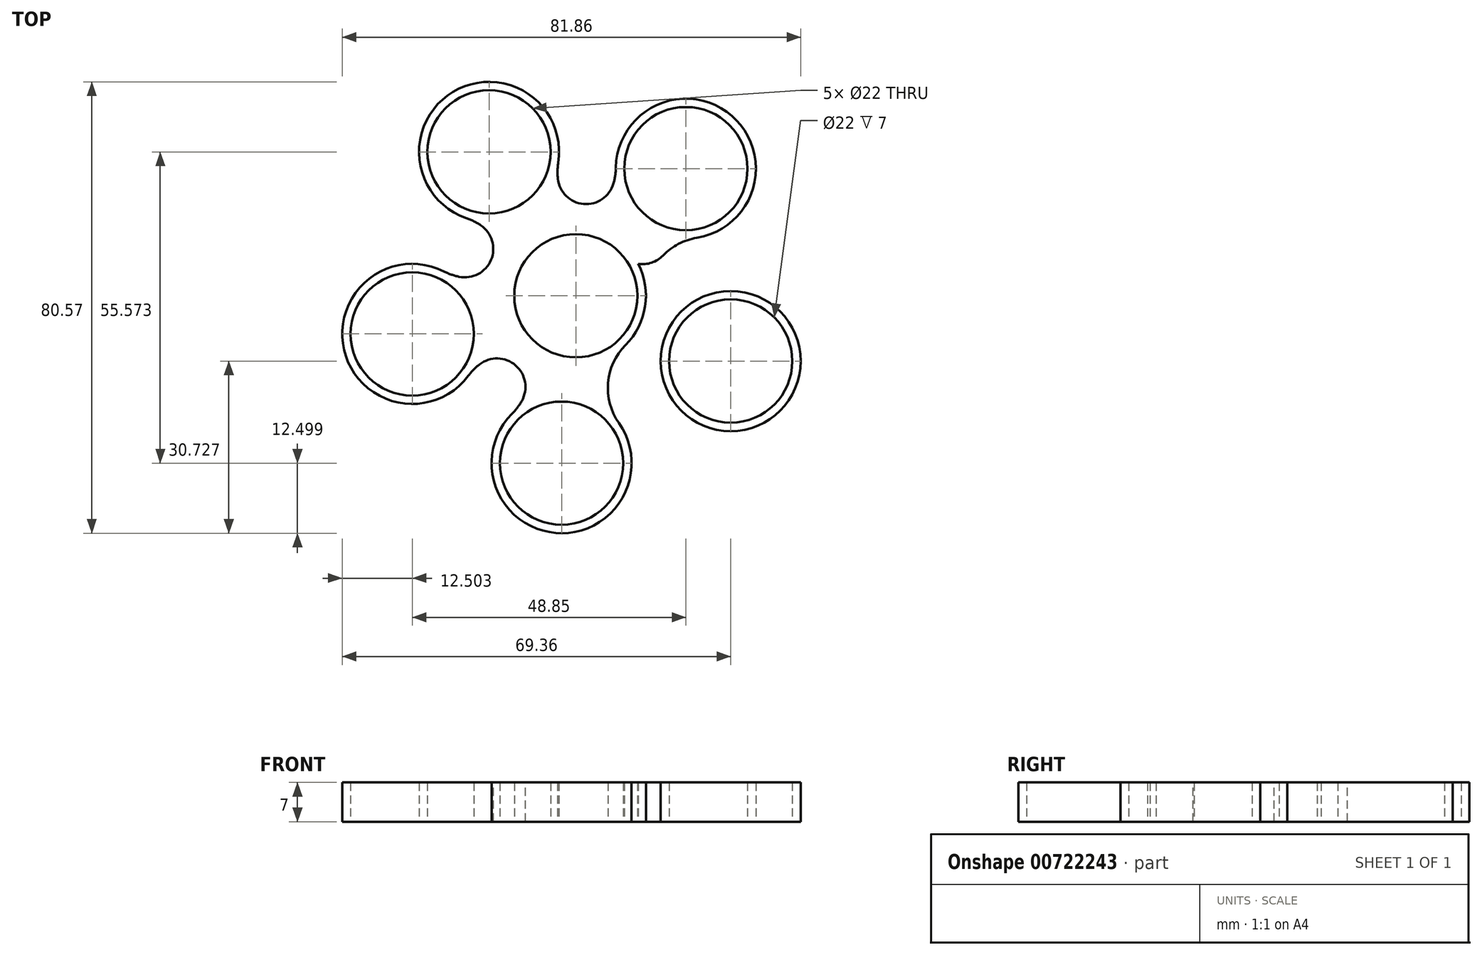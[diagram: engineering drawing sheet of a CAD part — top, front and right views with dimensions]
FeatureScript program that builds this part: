
annotation { "Feature Type Name" : "Feature", "Feature Type Description" : "" }
export const myFeature = defineFeature(function(context is Context, id is Id, definition is map)
    precondition{}
    {
        {
            var Q0;
            Q0=qCreatedBy(makeId("Top.planeOp"),FACE);
            var sketch = newSketch(context, id + "F0", { "sketchPlane" : qUnion([Q0])});
            skCircle(sketch, "E0", {"center": v(0, 0) * mm, "radius": 12.5 * mm});
            skCircle(sketch, "E1", {"center": v(19.63, 22.68) * mm, "radius": 12.5 * mm});
            skLineSegment(sketch, "E2", {"start": v(19.63, 22.68) * mm, "end": v(7.14, 22.87) * mm});
            skLineSegment(sketch, "E3", {"start": v(19.63, 22.68) * mm, "end": v(21.62, 10.34) * mm});
            skLineSegment(sketch, "E4", {"start": v(0, 0) * mm, "end": v(19.63, 22.68) * mm});
            skLineSegment(sketch, "E5", {"start": v(0, 0) * mm, "end": v(12.5, -0.2) * mm});
            skArc(sketch, "E6", {"start": v(21.62, 10.34) * mm, "mid": v(15.14, 6.73) * mm, "end": v(12.5, -0.2) * mm});
            skArc(sketch, "E7.MirrorCS", {"start": v(7.14, 22.87) * mm, "mid": v(4.5, 15.95) * mm, "end": v(-1.98, 12.34) * mm});
            skCircle(sketch, "E8", {"center": v(0, 0) * mm, "radius": 11 * mm});
            skCircle(sketch, "E9", {"center": v(19.63, 22.68) * mm, "radius": 11 * mm});
            skCircle(sketch, "E10.1.0", {"center": v(-15.5, 25.68) * mm, "radius": 11 * mm});
            skCircle(sketch, "E10.1.1", {"center": v(-15.5, 25.68) * mm, "radius": 12.5 * mm});
            skArc(sketch, "E10.1.2", {"start": v(-3.16, 23.75) * mm, "mid": v(-1.73, 16.48) * mm, "end": v(4.04, 11.83) * mm});
            skArc(sketch, "E10.1.3", {"start": v(-19.55, 13.85) * mm, "mid": v(-13.78, 9.2) * mm, "end": v(-12.35, 1.93) * mm});
            skCircle(sketch, "E10.2.0", {"center": v(-29.22, -6.81) * mm, "radius": 11 * mm});
            skCircle(sketch, "E10.2.1", {"center": v(-29.22, -6.81) * mm, "radius": 12.5 * mm});
            skArc(sketch, "E10.2.2", {"start": v(-23.57, 4.34) * mm, "mid": v(-16.2, 3.45) * mm, "end": v(-10, 7.5) * mm});
            skArc(sketch, "E10.2.3", {"start": v(-19.22, -14.31) * mm, "mid": v(-13.01, -10.26) * mm, "end": v(-5.65, -11.15) * mm});
            skCircle(sketch, "E10.3.0", {"center": v(-2.55, -29.9) * mm, "radius": 11 * mm});
            skCircle(sketch, "E10.3.1", {"center": v(-2.55, -29.9) * mm, "radius": 12.5 * mm});
            skArc(sketch, "E10.3.2", {"start": v(-11.4, -21.07) * mm, "mid": v(-8.3, -14.35) * mm, "end": v(-10.22, -7.2) * mm});
            skArc(sketch, "E10.3.3", {"start": v(7.67, -22.7) * mm, "mid": v(5.74, -15.54) * mm, "end": v(8.86, -8.82) * mm});
            skCircle(sketch, "E10.4.0", {"center": v(27.64, -11.66) * mm, "radius": 11 * mm});
            skCircle(sketch, "E10.4.1", {"center": v(27.64, -11.66) * mm, "radius": 12.5 * mm});
            skArc(sketch, "E10.4.2", {"start": v(16.51, -17.36) * mm, "mid": v(11.08, -12.32) * mm, "end": v(3.68, -11.95) * mm});
            skArc(sketch, "E10.4.3", {"start": v(23.96, 0.28) * mm, "mid": v(16.56, 0.65) * mm, "end": v(11.13, 5.7) * mm});
            skSolve(sketch);
        }
        {
            var Q0;
            {var subQ3=sQuery(id+"F0.wireOp",EDGE,"E7.MirrorCS");var subQ7=sQuery(id+"F0.wireOp",EDGE,"E0");var subQ8=makeQuery(id+"F0.imprint","INTERSECT",VERTEX,{"derivedFrom":[subQ7,subQ3]});Q0=makeQuery(id+"F0.imprint","IMPRINT",FACE,{"disambiguationData":[TD([[makeQuery(id+"F0.imprint","IMPRINT",EDGE,{"disambiguationData":[TD([[subQ8,-1.0]])],"derivedFrom":subQ7}),-1.0]])]});}
            var Q1;
            {var subQ1=sQuery(id+"F0.wireOp",EDGE,"E0");var subQ13=makeQuery(id+"F0.imprint","INTERSECT",VERTEX,{"derivedFrom":[subQ1,sQuery(id+"F0.wireOp",EDGE,"E10.1.2")]});Q1=makeQuery(id+"F0.imprint","IMPRINT",FACE,{"disambiguationData":[TD([[makeQuery(id+"F0.imprint","IMPRINT",EDGE,{"disambiguationData":[TD([[subQ13,1.0]])],"derivedFrom":subQ1}),1.0]])]});}
            var Q2;
            {var subQ0=sQuery(id+"F0.wireOp",EDGE,"E7.MirrorCS");var subQ1=sQuery(id+"F0.wireOp",EDGE,"E0");var subQ2=makeQuery(id+"F0.imprint","INTERSECT",VERTEX,{"derivedFrom":[subQ1,subQ0]});Q2=makeQuery(id+"F0.imprint","IMPRINT",FACE,{"disambiguationData":[TD([[makeQuery(id+"F0.imprint","IMPRINT",EDGE,{"disambiguationData":[TD([[subQ2,1.0]])],"derivedFrom":subQ1}),-1.0]])]});}
            var Q3;
            {var subQ1=sQuery(id+"F0.wireOp",EDGE,"E0");var subQ3=sQuery(id+"F0.wireOp",EDGE,"E10.4.3");var subQ4=makeQuery(id+"F0.imprint","INTERSECT",VERTEX,{"derivedFrom":[subQ1,subQ3]});Q3=makeQuery(id+"F0.imprint","IMPRINT",FACE,{"disambiguationData":[TD([[makeQuery(id+"F0.imprint","IMPRINT",EDGE,{"disambiguationData":[TD([[subQ4,1.0]])],"derivedFrom":subQ3}),1.0]])]});}
            var Q4;
            {var subQ1=sQuery(id+"F0.wireOp",EDGE,"E0");var subQ8=makeQuery(id+"F0.imprint","INTERSECT",VERTEX,{"derivedFrom":[subQ1,sQuery(id+"F0.wireOp",EDGE,"E10.4.3")]});Q4=makeQuery(id+"F0.imprint","IMPRINT",FACE,{"disambiguationData":[TD([[makeQuery(id+"F0.imprint","IMPRINT",EDGE,{"disambiguationData":[TD([[subQ8,-1.0]])],"derivedFrom":subQ1}),1.0]])]});}
            var Q5;
            {var subQ0=sQuery(id+"F0.wireOp",EDGE,"E10.1.3");var subQ1=sQuery(id+"F0.wireOp",EDGE,"E0");var subQ2=makeQuery(id+"F0.imprint","INTERSECT",VERTEX,{"derivedFrom":[subQ1,subQ0]});Q5=makeQuery(id+"F0.imprint","IMPRINT",FACE,{"disambiguationData":[TD([[makeQuery(id+"F0.imprint","IMPRINT",EDGE,{"disambiguationData":[TD([[subQ2,1.0]])],"derivedFrom":subQ1}),-1.0]])]});}
            var Q6;
            {var subQ3=sQuery(id+"F0.wireOp",EDGE,"E10.1.3");var subQ7=sQuery(id+"F0.wireOp",EDGE,"E0");var subQ8=makeQuery(id+"F0.imprint","INTERSECT",VERTEX,{"derivedFrom":[subQ7,subQ3]});Q6=makeQuery(id+"F0.imprint","IMPRINT",FACE,{"disambiguationData":[TD([[makeQuery(id+"F0.imprint","IMPRINT",EDGE,{"disambiguationData":[TD([[subQ8,-1.0]])],"derivedFrom":subQ7}),-1.0]])]});}
            var Q7;
            {var subQ5=sQuery(id+"F0.wireOp",EDGE,"E10.4.3");var subQ7=sQuery(id+"F0.wireOp",EDGE,"E0");var subQ9=makeQuery(id+"F0.imprint","INTERSECT",VERTEX,{"derivedFrom":[subQ7,subQ5]});Q7=makeQuery(id+"F0.imprint","IMPRINT",FACE,{"disambiguationData":[TD([[makeQuery(id+"F0.imprint","IMPRINT",EDGE,{"disambiguationData":[TD([[subQ9,-1.0]])],"derivedFrom":subQ7}),-1.0]])]});}
            var Q8;
            {var subQ6=sQuery(id+"F0.wireOp",EDGE,"E0");var subQ9=sQuery(id+"F0.wireOp",EDGE,"E10.3.3");var subQ10=makeQuery(id+"F0.imprint","INTERSECT",VERTEX,{"derivedFrom":[subQ6,subQ9]});Q8=makeQuery(id+"F0.imprint","IMPRINT",FACE,{"disambiguationData":[TD([[makeQuery(id+"F0.imprint","IMPRINT",EDGE,{"disambiguationData":[TD([[subQ10,1.0]])],"derivedFrom":subQ9}),-1.0]])]});}
            var Q9;
            {var subQ3=sQuery(id+"F0.wireOp",EDGE,"E10.1.2");var subQ5=sQuery(id+"F0.wireOp",EDGE,"E0");var subQ6=makeQuery(id+"F0.imprint","INTERSECT",VERTEX,{"derivedFrom":[subQ5,subQ3]});Q9=makeQuery(id+"F0.imprint","IMPRINT",FACE,{"disambiguationData":[TD([[makeQuery(id+"F0.imprint","IMPRINT",EDGE,{"disambiguationData":[TD([[subQ6,1.0]])],"derivedFrom":subQ5}),-1.0]])]});}
            var Q10;
            {var subQ0=sQuery(id+"F0.wireOp",EDGE,"E10.3.3");var subQ1=sQuery(id+"F0.wireOp",EDGE,"E0");var subQ2=makeQuery(id+"F0.imprint","INTERSECT",VERTEX,{"derivedFrom":[subQ1,subQ0]});Q10=makeQuery(id+"F0.imprint","IMPRINT",FACE,{"disambiguationData":[TD([[makeQuery(id+"F0.imprint","IMPRINT",EDGE,{"disambiguationData":[TD([[subQ2,1.0]])],"derivedFrom":subQ1}),-1.0]])]});}
            var Q11;
            {var subQ0=sQuery(id+"F0.wireOp",EDGE,"E10.2.3");var subQ1=sQuery(id+"F0.wireOp",EDGE,"E0");var subQ2=makeQuery(id+"F0.imprint","INTERSECT",VERTEX,{"derivedFrom":[subQ1,subQ0]});Q11=makeQuery(id+"F0.imprint","IMPRINT",FACE,{"disambiguationData":[TD([[makeQuery(id+"F0.imprint","IMPRINT",EDGE,{"disambiguationData":[TD([[subQ2,1.0]])],"derivedFrom":subQ1}),-1.0]])]});}
            var Q12;
            {var subQ3=sQuery(id+"F0.wireOp",EDGE,"E10.2.3");var subQ5=sQuery(id+"F0.wireOp",EDGE,"E0");var subQ6=makeQuery(id+"F0.imprint","INTERSECT",VERTEX,{"derivedFrom":[subQ5,subQ3]});Q12=makeQuery(id+"F0.imprint","IMPRINT",FACE,{"disambiguationData":[TD([[makeQuery(id+"F0.imprint","IMPRINT",EDGE,{"disambiguationData":[TD([[subQ6,-1.0]])],"derivedFrom":subQ5}),-1.0]])]});}
            var Q13;
            Q13=makeQuery(id+"F0.imprint","IMPRINT",FACE,{"disambiguationData":[TD([[makeQuery(id+"F0.imprint","IMPRINT",EDGE,{"derivedFrom":sQuery(id+"F0.wireOp",EDGE,"E10.4.0")}),-1.0]])]});
            var Q14;
            Q14=makeQuery(id+"F0.imprint","IMPRINT",FACE,{"disambiguationData":[TD([[makeQuery(id+"F0.imprint","IMPRINT",EDGE,{"derivedFrom":sQuery(id+"F0.wireOp",EDGE,"E10.3.0")}),-1.0]])]});
            var Q15;
            Q15=makeQuery(id+"F0.imprint","IMPRINT",FACE,{"disambiguationData":[TD([[makeQuery(id+"F0.imprint","IMPRINT",EDGE,{"derivedFrom":sQuery(id+"F0.wireOp",EDGE,"E10.2.0")}),-1.0]])]});
            var Q16;
            Q16=makeQuery(id+"F0.imprint","IMPRINT",FACE,{"disambiguationData":[TD([[makeQuery(id+"F0.imprint","IMPRINT",EDGE,{"derivedFrom":sQuery(id+"F0.wireOp",EDGE,"E10.1.0")}),-1.0]])]});
            var Q17;
            {var subQ0=sQuery(id+"F0.wireOp",EDGE,"E2");var subQ5=sQuery(id+"F0.wireOp",EDGE,"E9");var subQ6=makeQuery(id+"F0.imprint","INTERSECT",VERTEX,{"derivedFrom":[subQ0,subQ5]});Q17=makeQuery(id+"F0.imprint","IMPRINT",FACE,{"disambiguationData":[TD([[makeQuery(id+"F0.imprint","IMPRINT",EDGE,{"disambiguationData":[TD([[subQ6,1.0]])],"derivedFrom":subQ5}),-1.0]])]});}
            var Q18;
            {var subQ1=sQuery(id+"F0.wireOp",EDGE,"E1");var subQ3=sQuery(id+"F0.wireOp",EDGE,"E4");var subQ4=makeQuery(id+"F0.imprint","INTERSECT",VERTEX,{"derivedFrom":[subQ1,subQ3]});Q18=makeQuery(id+"F0.imprint","IMPRINT",FACE,{"disambiguationData":[TD([[makeQuery(id+"F0.imprint","IMPRINT",EDGE,{"disambiguationData":[TD([[subQ4,-1.0]])],"derivedFrom":subQ3}),1.0]])]});}
            var Q19;
            {var subQ1=sQuery(id+"F0.wireOp",EDGE,"E1");var subQ3=sQuery(id+"F0.wireOp",EDGE,"E4");var subQ4=makeQuery(id+"F0.imprint","INTERSECT",VERTEX,{"derivedFrom":[subQ1,subQ3]});Q19=makeQuery(id+"F0.imprint","IMPRINT",FACE,{"disambiguationData":[TD([[makeQuery(id+"F0.imprint","IMPRINT",EDGE,{"disambiguationData":[TD([[subQ4,-1.0]])],"derivedFrom":subQ3}),-1.0]])]});}
            extrude(context, id + "F1", {"entities" : qUnion([Q0, Q1, Q2, Q3, Q4, Q5, Q6, Q7, Q8, Q9, Q10, Q11, Q12, Q13, Q14, Q15, Q16, Q17, Q18, Q19]), "depth" : 7 * mm, "offsetDistance" : 25.4 * mm});
        }
        {
            var Q0;
            Q0=makeQuery(id+"F1.opExtrude","SWEPT_EDGE",EDGE,{"disambiguationData":[OSD([sQuery(id+"F0.wireOp",EDGE,"E10.3.3"),sQuery(id+"F0.wireOp",EDGE,"E10.4.2")])]});
            var Q1;
            Q1=makeQuery(id+"F1.opExtrude","SWEPT_EDGE",EDGE,{"disambiguationData":[OSD([sQuery(id+"F0.wireOp",EDGE,"E10.2.3"),sQuery(id+"F0.wireOp",EDGE,"E10.3.2")])]});
            var Q2;
            Q2=makeQuery(id+"F1.opExtrude","SWEPT_EDGE",EDGE,{"disambiguationData":[OSD([sQuery(id+"F0.wireOp",EDGE,"E10.1.3"),sQuery(id+"F0.wireOp",EDGE,"E10.2.2")])]});
            var Q3;
            Q3=makeQuery(id+"F1.opExtrude","SWEPT_EDGE",EDGE,{"disambiguationData":[OSD([sQuery(id+"F0.wireOp",EDGE,"E7.MirrorCS"),sQuery(id+"F0.wireOp",EDGE,"E10.1.2")])]});
            var Q4;
            Q4=makeQuery(id+"F1.opExtrude","SWEPT_EDGE",EDGE,{"disambiguationData":[OSD([sQuery(id+"F0.wireOp",EDGE,"E6"),sQuery(id+"F0.wireOp",EDGE,"E10.4.3")])]});
            fillet(context, id + "F2", {"entities" : qUnion([Q0, Q1, Q2, Q3, Q4]), "radius" : 5.08 * mm, "tangentPropagation" : true, "allowEdgeOverflow" : false});
        }
    });
